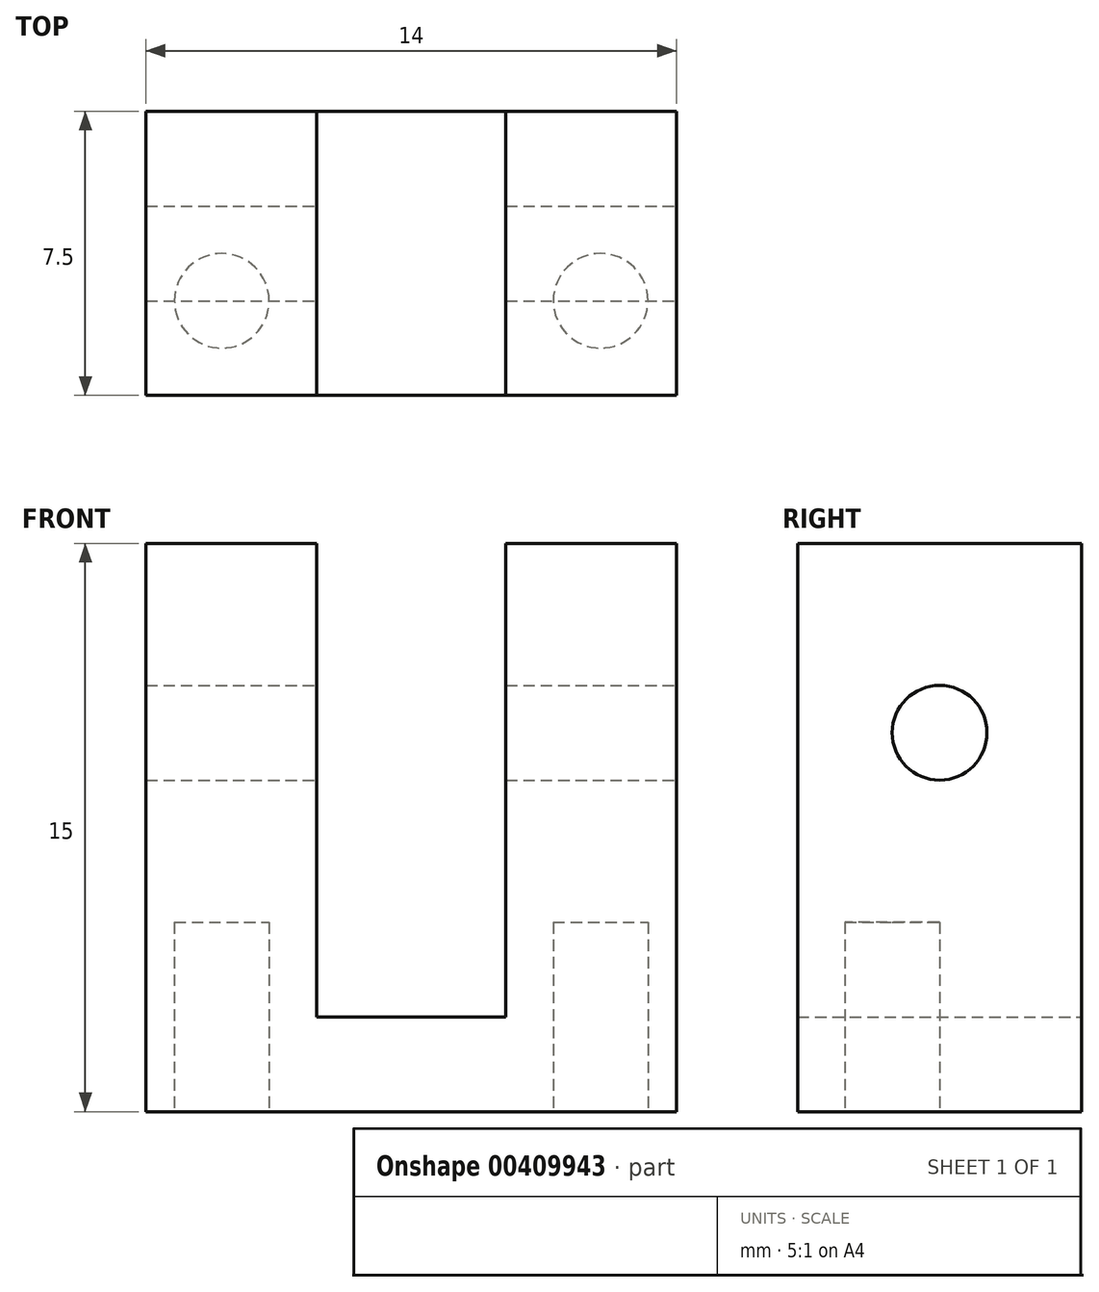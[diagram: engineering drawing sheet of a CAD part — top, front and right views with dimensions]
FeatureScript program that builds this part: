
annotation { "Feature Type Name" : "Feature", "Feature Type Description" : "" }
export const myFeature = defineFeature(function(context is Context, id is Id, definition is map)
    precondition{}
    {
        {
            var Q0;
            Q0=qCreatedBy(makeId("Front.planeOp"),FACE);
            var sketch = newSketch(context, id + "F0", { "sketchPlane" : qUnion([Q0])});
            skLineSegment(sketch, "E0.bottom", {"start": v(0, 0) * mm, "end": v(14, 0) * mm});
            skLineSegment(sketch, "E0.top", {"start": v(0, 15) * mm, "end": v(4.5, 15) * mm});
            skLineSegment(sketch, "E0.left", {"start": v(0, 0) * mm, "end": v(0, 15) * mm});
            skLineSegment(sketch, "E0.right", {"start": v(14, 0) * mm, "end": v(14, 15) * mm});
            skLineSegment(sketch, "E1.top", {"start": v(4.5, 2.5) * mm, "end": v(9.5, 2.5) * mm});
            skLineSegment(sketch, "E1.left", {"start": v(4.5, 15) * mm, "end": v(4.5, 2.5) * mm});
            skLineSegment(sketch, "E1.right", {"start": v(9.5, 15) * mm, "end": v(9.5, 2.5) * mm});
            skLineSegment(sketch, "E2.trimOffspring", {"start": v(9.5, 15) * mm, "end": v(14, 15) * mm});
            skSolve(sketch);
        }
        {
            var Q0;
            Q0=makeQuery(id+"F0.imprint","IMPRINT",FACE,{"disambiguationData":[TD([[makeQuery(id+"F0.imprint","IMPRINT",EDGE,{"derivedFrom":sQuery(id+"F0.wireOp",EDGE,"E0.bottom")}),1.0]])]});
            extrude(context, id + "F1", {"entities" : qUnion([Q0]), "depth" : 7.5 * mm});
        }
        {
            var Q0;
            Q0=makeQuery(id+"F1.opExtrude","SWEPT_FACE",FACE,{"disambiguationData":[OSD([sQuery(id+"F0.wireOp",EDGE,"E0.right")])]});
            var sketch = newSketch(context, id + "F2", { "sketchPlane" : qUnion([Q0])});
            skCircle(sketch, "E3", {"center": v(-3.75, 10) * mm, "radius": 1.25 * mm});
            skSolve(sketch);
        }
        {
            var Q0;
            Q0=makeQuery(id+"F2.imprint","IMPRINT",FACE,{"disambiguationData":[TD([[makeQuery(id+"F2.imprint","IMPRINT",EDGE,{"derivedFrom":sQuery(id+"F2.wireOp",EDGE,"E3")}),1.0]])]});
            extrude(context, id + "F3", {"entities" : qUnion([Q0]), "operationType" : NewBodyOperationType.REMOVE, "oppositeDirection" : true, "depth" : 25 * mm});
        }
        {
            var Q0;
            Q0=makeQuery(id+"F1.opExtrude","SWEPT_FACE",FACE,{"disambiguationData":[OSD([sQuery(id+"F0.wireOp",EDGE,"E0.bottom")])]});
            var sketch = newSketch(context, id + "F4", { "sketchPlane" : qUnion([Q0])});
            skCircle(sketch, "E4", {"center": v(2, 5) * mm, "radius": 1.25 * mm});
            skCircle(sketch, "E5", {"center": v(12, 5) * mm, "radius": 1.25 * mm});
            skSolve(sketch);
        }
        {
            var Q0;
            Q0=makeQuery(id+"F4.imprint","IMPRINT",FACE,{"disambiguationData":[TD([[makeQuery(id+"F4.imprint","IMPRINT",EDGE,{"derivedFrom":sQuery(id+"F4.wireOp",EDGE,"E4")}),1.0]])]});
            var Q1;
            Q1=makeQuery(id+"F4.imprint","IMPRINT",FACE,{"disambiguationData":[TD([[makeQuery(id+"F4.imprint","IMPRINT",EDGE,{"derivedFrom":sQuery(id+"F4.wireOp",EDGE,"E5")}),1.0]])]});
            extrude(context, id + "F5", {"entities" : qUnion([Q0, Q1]), "operationType" : NewBodyOperationType.REMOVE, "oppositeDirection" : true, "depth" : 5 * mm});
        }
    });
